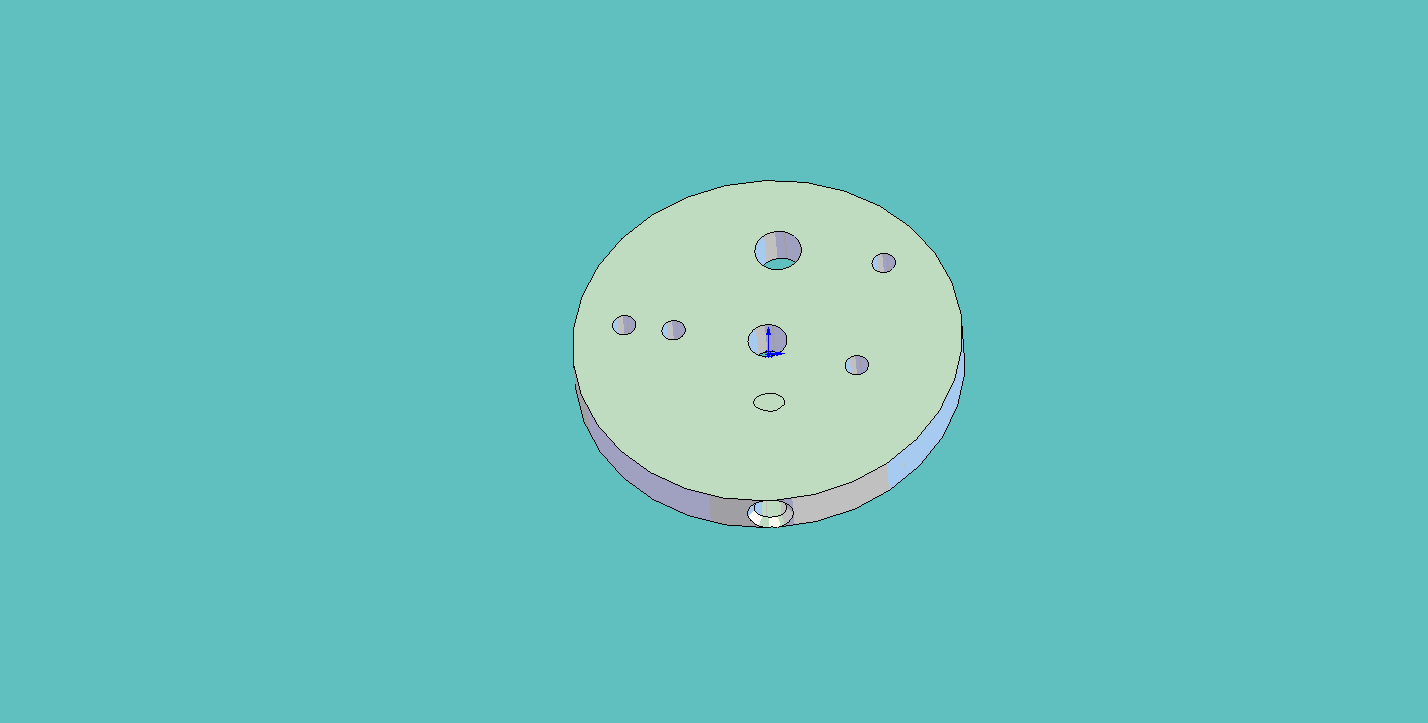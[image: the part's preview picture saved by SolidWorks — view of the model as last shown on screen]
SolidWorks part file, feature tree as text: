
SOLIDWORKS PART (.sldprt)
format: sldprt  version: not decoded by parser v0  size: 186,368 bytes
history: native  units: mm
features: sketch x4, plane x3, material x1, extrude x1, cut_revolve x1, hole x1, thread x1 (+8 scaffold rows collapsed)
feature tree (20):
  scaffold x8  (default folders/planes/origin — collapsed)
  material  "Matériau <non spécifié>"
  plane  "Plan de face"
  plane  "Plan de dessus"
  plane  "Plan de droite"
  sketch  "Esquisse1"  dims[c1.D1=3.0mm c1.D2=5.0mm c1.D3=5.98mm c1.D4=50.0mm c1.D5=3.0mm c1.D6=3.0mm c1.D7=3.0mm c1.D8=3.0mm c1.D9=3.0mm c1.D10=5.98mm c1.D12=3.0mm c1.D13=3.0mm c1.D14=3.0mm c1.D15=3.0mm c2.D5=2.2mm c2.D6=12.0mm c2.D8=18.3mm c2.D9=3.3mm c2.D10=14.0mm c2.D11=1.5mm c2.D12=11.4mm c2.D13=15.0mm c2.D14=11.4mm c2.D15=4.4mm]
  extrude  "Extrusion1"  Depth=6mm
  sketch  "Esquisse2"  dims[c1.D1=4.2mm c1.D2=17.5mm c1.D3=1.0mm c1.D4=~0.678497mm c2.D3=~3.680262mm c3.D3=45.0deg c3.D4=1.0mm]
  cut_revolve  "Enlèvement de matière-Révolution1"  Angle=360deg
  hole  "Trou taraudé M4x0.71"  Diameter=3.3mm Depth=7.5mm
  sketch  "Esquisse3D1"
  sketch  "Esquisse3"  dims[hole-wizard template sketch: 47 standard entries collapsed; hole parameters kept: c15.Profondeur du trou pour taraudage=7.5mm c15.D3=~14.816244mm c15.Angle de pointe=118.0deg]
  thread  "Filetage de perçage1"  Diameter=5.621836mm  [1 undecoded]
decode coverage: 7 of 8 modeling features carry decoded parameters
note: ~ marks probable driven/reference dimensions
note: 1 parameter value undecoded
note: suppression state not decoded; provenance and decode notes live in map.json
